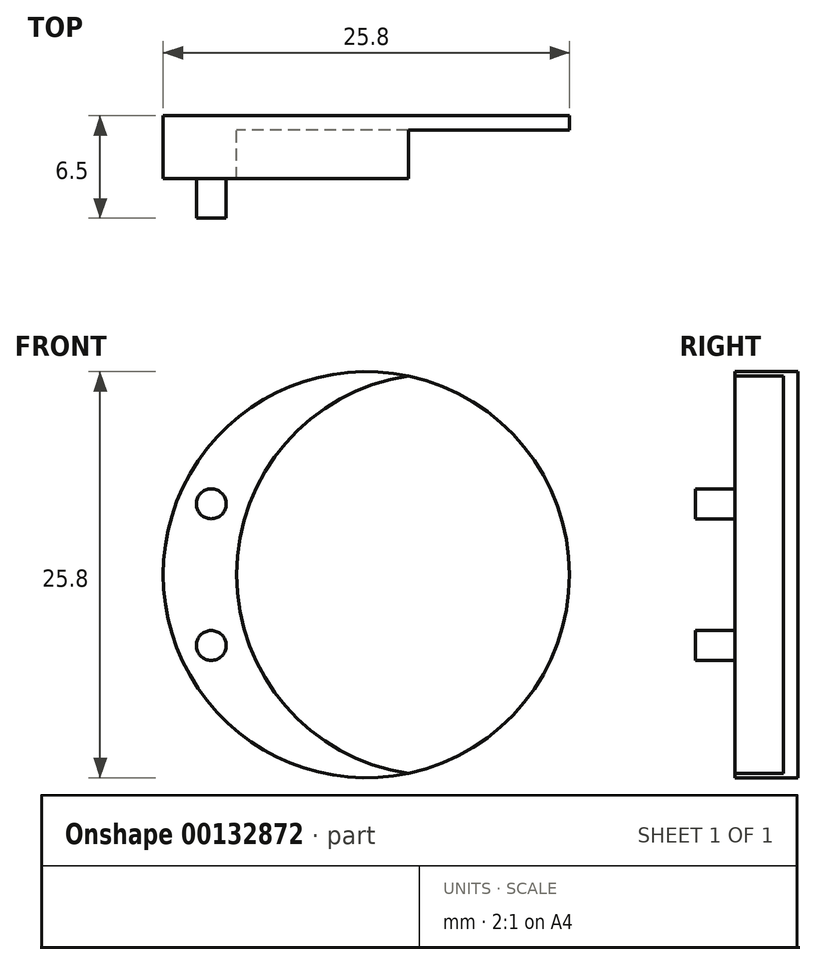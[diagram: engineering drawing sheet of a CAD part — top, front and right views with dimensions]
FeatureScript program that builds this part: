
annotation { "Feature Type Name" : "Feature", "Feature Type Description" : "" }
export const myFeature = defineFeature(function(context is Context, id is Id, definition is map)
    precondition{}
    {
        {
            var Q0;
            Q0=qCreatedBy(makeId("Front.planeOp"),FACE);
            var sketch = newSketch(context, id + "F0", { "sketchPlane" : qUnion([Q0])});
            skCircle(sketch, "E0", {"center": v(0, 0) * mm, "radius": 12.9 * mm});
            skSolve(sketch);
        }
        {
            var Q0;
            Q0 = qSketchRegion(id + "F0", true);
            extrude(context, id + "F1", {"entities" : qUnion([Q0]), "depth" : 0.9 * mm});
        }
        {
            var Q0;
            Q0=makeQuery(id+"F1.opExtrude","CAP_FACE",FACE,{"disambiguationData":[OSD([sQuery(id+"F0.wireOp",EDGE,"E0")])],"isStart":false});
            var sketch = newSketch(context, id + "F2", { "sketchPlane" : qUnion([Q0])});
            skArc(sketch, "E1", {"start": v(2.68, 12.62) * mm, "mid": v(-8.25, 0) * mm, "end": v(2.68, -12.62) * mm});
            skArc(sketch, "E2", {"start": v(2.68, 12.62) * mm, "mid": v(-12.9, 0) * mm, "end": v(2.68, -12.62) * mm});
            skSolve(sketch);
        }
        {
            var Q0;
            Q0 = qSketchRegion(id + "F2", true);
            extrude(context, id + "F3", {"entities" : qUnion([Q0]), "operationType" : NewBodyOperationType.ADD, "depth" : 3.1 * mm});
        }
        {
            var Q0;
            Q0=makeQuery(id+"F3.opExtrude","CAP_FACE",FACE,{"disambiguationData":[OSD([sQuery(id+"F2.wireOp",EDGE,"E1"),sQuery(id+"F2.wireOp",EDGE,"E2")])],"isStart":false});
            var sketch = newSketch(context, id + "F4", { "sketchPlane" : qUnion([Q0])});
            skCircle(sketch, "E3", {"center": v(-9.85, 4.5) * mm, "radius": 0.95 * mm});
            skLineSegment(sketch, "E4", {"start": v(-28.48, 0) * mm, "end": v(17.9, 0) * mm, "construction": true});
            skCircle(sketch, "E5.MirrorC", {"center": v(-9.85, -4.5) * mm, "radius": 0.95 * mm});
            skSolve(sketch);
        }
        {
            var Q0;
            Q0 = qSketchRegion(id + "F4", true);
            extrude(context, id + "F5", {"entities" : qUnion([Q0]), "operationType" : NewBodyOperationType.ADD, "depth" : 2.5 * mm});
        }
    });
